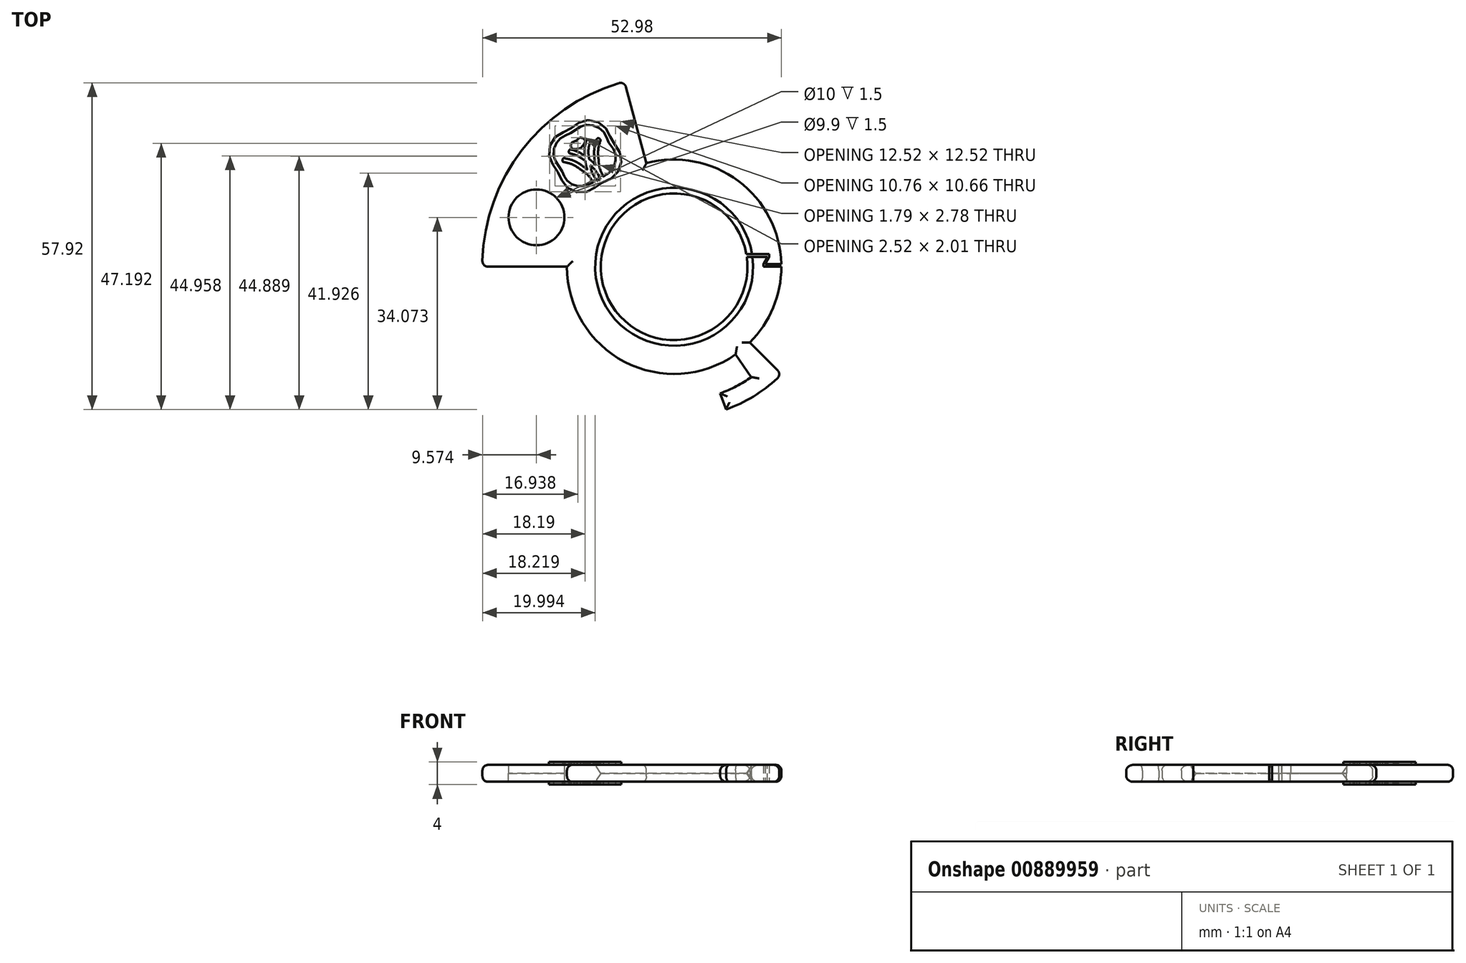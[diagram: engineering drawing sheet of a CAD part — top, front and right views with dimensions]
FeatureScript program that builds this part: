
annotation { "Feature Type Name" : "Feature", "Feature Type Description" : "" }
export const myFeature = defineFeature(function(context is Context, id is Id, definition is map)
    precondition{}
    {
        {
            var Q0;
            Q0=qCreatedBy(makeId("Front.planeOp"),FACE);
            var sketch = newSketch(context, id + "F0", { "sketchPlane" : qUnion([Q0])});
            skLineSegment(sketch, "E0.bottom", {"start": v(-19, 1.5) * mm, "end": v(-14, 1.5) * mm});
            skLineSegment(sketch, "E0.top", {"start": v(-19, 0) * mm, "end": v(-13.96, 0) * mm});
            skLineSegment(sketch, "E0.left", {"start": v(-19, 1.5) * mm, "end": v(-19, 0) * mm});
            skLineSegment(sketch, "E1", {"start": v(-14, 1.5) * mm, "end": v(-13, 0) * mm});
            skLineSegment(sketch, "E2", {"start": v(-13, 0) * mm, "end": v(-13.96, 0) * mm});
            skLineSegment(sketch, "E3.MirrorCS", {"start": v(-19, -1.5) * mm, "end": v(-19, 0) * mm});
            skLineSegment(sketch, "E4.MirrorCS", {"start": v(-19, -1.5) * mm, "end": v(-14, -1.5) * mm});
            skLineSegment(sketch, "E5.MirrorCS", {"start": v(-14, -1.5) * mm, "end": v(-13, 0) * mm});
            skSolve(sketch);
        }
        {
            var Q0;
            Q0=qCreatedBy(makeId("Right.planeOp"),FACE);
            var sketch = newSketch(context, id + "F1", { "sketchPlane" : qUnion([Q0])});
            skLineSegment(sketch, "E6", {"start": v(0, -35.32) * mm, "end": v(0, 30.2) * mm});
            skSolve(sketch);
        }
        {
            var Q0;
            Q0 = qSketchRegion(id + "F0", true);
            var Q1;
            Q1=sQuery(id+"F1.wireOp",EDGE,"E6");
            revolve(context, id + "F2", {"surfaceOperationType" : NewSurfaceOperationType.NEW, "entities" : qUnion([Q0]), "axis" : qUnion([Q1]), "revolveType" : RevolveType.FULL});
        }
        {
            var Q0;
            Q0=qCreatedBy(makeId("Front.planeOp"),FACE);
            var sketch = newSketch(context, id + "F3", { "sketchPlane" : qUnion([Q0])});
            skLineSegment(sketch, "E7.bottom", {"start": v(-34, -1.5) * mm, "end": v(-19, -1.5) * mm});
            skLineSegment(sketch, "E7.top", {"start": v(-34, 1.5) * mm, "end": v(-19, 1.5) * mm});
            skLineSegment(sketch, "E7.left", {"start": v(-34, -1.5) * mm, "end": v(-34, 1.5) * mm});
            skLineSegment(sketch, "E7.right", {"start": v(-19, -1.5) * mm, "end": v(-19, 1.5) * mm});
            skLineSegment(sketch, "E8", {"start": v(19, 1.5) * mm, "end": v(19, -1.5) * mm});
            skSolve(sketch);
        }
        {
            var Q0;
            Q0=qCreatedBy(makeId("Right.planeOp"),FACE);
            var sketch = newSketch(context, id + "F4", { "sketchPlane" : qUnion([Q0])});
            skLineSegment(sketch, "E9", {"start": v(0, 18.48) * mm, "end": v(0, -14.6) * mm});
            skSolve(sketch);
        }
        {
            var Q0;
            Q0 = qSketchRegion(id + "F3", true);
            var Q1;
            Q1=sQuery(id+"F4.wireOp",EDGE,"E9");
            revolve(context, id + "F5", {"operationType" : NewBodyOperationType.ADD, "surfaceOperationType" : NewSurfaceOperationType.NEW, "entities" : qUnion([Q0]), "axis" : qUnion([Q1]), "revolveType" : RevolveType.ONE_DIRECTION, "angle" : 75 * degree});
        }
        {
            var Q0;
            Q0=qCreatedBy(makeId("Top.planeOp"),FACE);
            var sketch = newSketch(context, id + "F6", { "sketchPlane" : qUnion([Q0])});
            skCircle(sketch, "E10", {"center": v(-24.4, 8.75) * mm, "radius": 5 * mm});
            skSolve(sketch);
        }
        {
            var Q0;
            Q0=makeQuery(id+"F5.boolean.opBoolean","MERGE",FACE,{"derivedFrom":[makeQuery(id+"F2.opRevolve","SWEPT_FACE",FACE,{"disambiguationData":[OSD([sQuery(id+"F0.wireOp",EDGE,"E0.bottom")])]}),makeQuery(id+"F5.opRevolve","SWEPT_FACE",FACE,{"disambiguationData":[OSD([sQuery(id+"F3.wireOp",EDGE,"E7.top")])]})]});
            var sketch = newSketch(context, id + "F7", { "sketchPlane" : qUnion([Q0])});
            skLineSegment(sketch, "E11", {"start": v(19, 0) * mm, "end": v(15.82, 0) * mm});
            skLineSegment(sketch, "E12", {"start": v(15.82, 0) * mm, "end": v(16.84, 1.72) * mm});
            skLineSegment(sketch, "E13", {"start": v(16.84, 1.72) * mm, "end": v(11.15, 1.72) * mm});
            skSolve(sketch);
        }
        {
            var Q0;
            Q0 = qSketchRegion(id + "F7", true);
            var Q1;
            Q1=sQuery(id+"F7.wireOp",EDGE,"E13");
            var Q2;
            Q2=sQuery(id+"F7.wireOp",EDGE,"E12");
            var Q3;
            Q3=sQuery(id+"F7.wireOp",EDGE,"E11");
            var Q4;
            Q4=sQuery(id+"F7.wireOp",EDGE,"dRNst7FH-cN4A-1J2b-OH71-uqqUjtxT50Xl");
            extrude(context, id + "F8", {"entities" : qUnion([Q0]), "bodyType" : ToolBodyType.SURFACE, "surfaceEntities" : qUnion([Q1, Q2, Q3, Q4]), "endBound" : BoundingType.SYMMETRIC, "oppositeDirection" : true, "depth" : 18.2 * mm, "offsetDistance" : 25 * mm});
        }
        {
            var Q0;
            Q0=qCreatedBy(makeId("Front.planeOp"),FACE);
            var Q1;
            Q1=qCreatedBy(makeId("Right.planeOp"),FACE);
            cPlane(context, id + "F9", {"entities" : qUnion([Q0, Q1]), "cplaneType" : CPlaneType.MID_PLANE, "offset" : 25 * mm, "width" : 150 * mm, "height" : 150 * mm});
        }
        {
            var Q0;
            Q0=qCreatedBy(id+"F9.planeOp",FACE);
            var sketch = newSketch(context, id + "F10", { "sketchPlane" : qUnion([Q0])});
            skLineSegment(sketch, "E14.bottom", {"start": v(18.75, 1.5) * mm, "end": v(26.94, 1.5) * mm});
            skLineSegment(sketch, "E14.top", {"start": v(18.75, -1.5) * mm, "end": v(26.94, -1.5) * mm});
            skLineSegment(sketch, "E14.left", {"start": v(18.75, 1.5) * mm, "end": v(18.75, -1.5) * mm});
            skLineSegment(sketch, "E14.right", {"start": v(26.94, 1.5) * mm, "end": v(26.94, -1.5) * mm});
            skLineSegment(sketch, "E15", {"start": v(23.89, 1.5) * mm, "end": v(23.89, -1.5) * mm});
            skSolve(sketch);
        }
        {
            var Q0;
            Q0=qCreatedBy(makeId("Front.planeOp"),FACE);
            var sketch = newSketch(context, id + "F11", { "sketchPlane" : qUnion([Q0])});
            skLineSegment(sketch, "E16", {"start": v(0, -32.03) * mm, "end": v(0, 34.42) * mm});
            skSolve(sketch);
        }
        {
            var Q0;
            {var subQ0=sQuery(id+"F10.wireOp",EDGE,"E14.left");Q0=makeQuery(id+"F10.imprint","IMPRINT",FACE,{"disambiguationData":[TD([[makeQuery(id+"F10.imprint","IMPRINT",EDGE,{"derivedFrom":subQ0}),1.0]])]});}
            var Q1;
            Q1=sQuery(id+"F11.wireOp",EDGE,"E16");
            revolve(context, id + "F12", {"operationType" : NewBodyOperationType.ADD, "surfaceOperationType" : NewSurfaceOperationType.NEW, "entities" : qUnion([Q0]), "axis" : qUnion([Q1]), "revolveType" : RevolveType.ONE_DIRECTION, "oppositeDirection" : true, "angle" : 10 * degree});
        }
        {
            var Q0;
            {var subQ0=sQuery(id+"F10.wireOp",EDGE,"E14.right");Q0=makeQuery(id+"F10.imprint","IMPRINT",FACE,{"disambiguationData":[TD([[makeQuery(id+"F10.imprint","IMPRINT",EDGE,{"derivedFrom":subQ0}),-1.0]])]});}
            var Q1;
            Q1=sQuery(id+"F11.wireOp",EDGE,"E16");
            revolve(context, id + "F13", {"operationType" : NewBodyOperationType.ADD, "surfaceOperationType" : NewSurfaceOperationType.NEW, "entities" : qUnion([Q0]), "axis" : qUnion([Q1]), "revolveType" : RevolveType.ONE_DIRECTION, "oppositeDirection" : true, "angle" : 25 * degree});
        }
        {
            var Q0;
            Q0=makeQuery(id+"F8.opExtrude","SWEPT_FACE",FACE,{"disambiguationData":[OSD([sQuery(id+"F7.wireOp",EDGE,"E13")])]});
            var Q1;
            Q1=makeQuery(id+"F8.opExtrude","SWEPT_FACE",FACE,{"disambiguationData":[OSD([sQuery(id+"F7.wireOp",EDGE,"E12")])]});
            var Q2;
            Q2=makeQuery(id+"F8.opExtrude","SWEPT_FACE",FACE,{"disambiguationData":[OSD([sQuery(id+"F7.wireOp",EDGE,"E11"),sQuery(id+"F7.wireOp",EDGE,"dRNst7FH-cN4A-1J2b-OH71-uqqUjtxT50Xl")])]});
            extrude(context, id + "F14", {"entities" : qUnion([Q0, Q1, Q2]), "operationType" : NewBodyOperationType.REMOVE, "oppositeDirection" : true, "depth" : 0.5 * mm, "offsetDistance" : 25 * mm});
        }
        {
            var Q0;
            Q0=sQuery(id+"F6.wireOp",VERTEX,"E10.center");
            var Q1;
            Q1=makeQuery(id+"F2.opRevolve","SWEPT_BODY",BODY,{"disambiguationData":[OSD([sQuery(id+"F0.wireOp",EDGE,"E0.bottom"),sQuery(id+"F0.wireOp",EDGE,"E0.left"),sQuery(id+"F0.wireOp",EDGE,"E1"),sQuery(id+"F0.wireOp",EDGE,"E3.MirrorCS"),sQuery(id+"F0.wireOp",EDGE,"E4.MirrorCS"),sQuery(id+"F0.wireOp",EDGE,"E5.MirrorCS")])]});
            hole(context, id + "F15", {"style" : HoleStyle.SIMPLE, "endStyle" : HoleEndStyle.THROUGH, "holeDiameter" : 10 * mm, "majorDiameter" : 5 * mm, "isTappedThrough" : true, "tappedDepth" : 12 * mm, "tapClearance" : 3, "locations" : qUnion([Q0]), "scope" : qUnion([Q1])});
        }
        {
            var Q0;
            Q0=sQuery(id+"F6.wireOp",VERTEX,"E10.center");
            var Q1;
            Q1=makeQuery(id+"F2.opRevolve","SWEPT_BODY",BODY,{"disambiguationData":[OSD([sQuery(id+"F0.wireOp",EDGE,"E0.bottom"),sQuery(id+"F0.wireOp",EDGE,"E0.left"),sQuery(id+"F0.wireOp",EDGE,"E1"),sQuery(id+"F0.wireOp",EDGE,"E3.MirrorCS"),sQuery(id+"F0.wireOp",EDGE,"E4.MirrorCS"),sQuery(id+"F0.wireOp",EDGE,"E5.MirrorCS")])]});
            hole(context, id + "F16", {"style" : HoleStyle.SIMPLE, "endStyle" : HoleEndStyle.THROUGH, "oppositeDirection" : true, "holeDiameter" : 9.9 * mm, "majorDiameter" : 5 * mm, "isTappedThrough" : true, "tappedDepth" : 12 * mm, "tapClearance" : 3, "locations" : qUnion([Q0]), "scope" : qUnion([Q1])});
        }
        {
            var Q0;
            Q0=makeQuery(id+"F5.opRevolve","CAP_EDGE",EDGE,{"disambiguationData":[OSD([sQuery(id+"F3.wireOp",EDGE,"E7.top")])],"isStart":true});
            var Q1;
            Q1=makeQuery(id+"F5.opRevolve","SWEPT_EDGE",EDGE,{"disambiguationData":[OSD([sQuery(id+"F3.wireOp",EDGE,"E7.top"),sQuery(id+"F3.wireOp",EDGE,"E7.left")])]});
            var Q2;
            Q2=makeQuery(id+"F5.opRevolve","CAP_EDGE",EDGE,{"disambiguationData":[OSD([sQuery(id+"F3.wireOp",EDGE,"E7.top")])],"isStart":false});
            var Q3;
            Q3=makeQuery(id+"F5.opRevolve","CAP_EDGE",EDGE,{"disambiguationData":[OSD([sQuery(id+"F3.wireOp",EDGE,"E7.bottom")])],"isStart":false});
            var Q4;
            Q4=makeQuery(id+"F5.opRevolve","SWEPT_EDGE",EDGE,{"disambiguationData":[OSD([sQuery(id+"F3.wireOp",EDGE,"E7.bottom"),sQuery(id+"F3.wireOp",EDGE,"E7.left")])]});
            var Q5;
            Q5=makeQuery(id+"F5.opRevolve","CAP_EDGE",EDGE,{"disambiguationData":[OSD([sQuery(id+"F3.wireOp",EDGE,"E7.bottom")])],"isStart":true});
            var Q6;
            {var subQ0=sQuery(id+"F3.wireOp",EDGE,"E7.top");var subQ1=sQuery(id+"F0.wireOp",EDGE,"E0.left");var subQ2=sQuery(id+"F0.wireOp",EDGE,"E0.bottom");Q6=makeQuery(id+"F12.boolean.opBoolean","SPLIT",EDGE,{"disambiguationData":[TD([makeQuery(id+"F5.opRevolve","CAP_FACE",FACE,{"disambiguationData":[OSD([sQuery(id+"F3.wireOp",EDGE,"E7.bottom"),subQ0,sQuery(id+"F3.wireOp",EDGE,"E7.left"),sQuery(id+"F3.wireOp",EDGE,"E7.right")])],"isStart":true})])],"derivedFrom":makeQuery(id+"F2.opRevolve","SWEPT_EDGE",EDGE,{"disambiguationData":[OSD([subQ2,subQ1])]})});}
            var Q7;
            {var subQ0=sQuery(id+"F3.wireOp",EDGE,"E7.bottom");var subQ1=sQuery(id+"F0.wireOp",EDGE,"E4.MirrorCS");var subQ2=sQuery(id+"F0.wireOp",EDGE,"E3.MirrorCS");Q7=makeQuery(id+"F12.boolean.opBoolean","SPLIT",EDGE,{"disambiguationData":[TD([makeQuery(id+"F5.opRevolve","CAP_FACE",FACE,{"disambiguationData":[OSD([subQ0,sQuery(id+"F3.wireOp",EDGE,"E7.top"),sQuery(id+"F3.wireOp",EDGE,"E7.left"),sQuery(id+"F3.wireOp",EDGE,"E7.right")])],"isStart":true})])],"derivedFrom":makeQuery(id+"F2.opRevolve","SWEPT_EDGE",EDGE,{"disambiguationData":[OSD([subQ2,subQ1])]})});}
            var Q8;
            {var subQ0=sQuery(id+"F3.wireOp",EDGE,"E7.top");var subQ2=makeQuery(id+"F5.opRevolve","CAP_FACE",FACE,{"disambiguationData":[OSD([sQuery(id+"F3.wireOp",EDGE,"E7.bottom"),subQ0,sQuery(id+"F3.wireOp",EDGE,"E7.left"),sQuery(id+"F3.wireOp",EDGE,"E7.right")])],"isStart":false});var subQ3=sQuery(id+"F0.wireOp",EDGE,"E0.left");var subQ5=sQuery(id+"F0.wireOp",EDGE,"E0.bottom");Q8=makeQuery(id+"F14.boolean.opBoolean","SPLIT",EDGE,{"disambiguationData":[TD([makeQuery(id+"F14.opExtrude","CAP_FACE",FACE,{"disambiguationData":[OSD([sQuery(id+"F7.wireOp",EDGE,"E11")])],"isStart":false})])],"derivedFrom":makeQuery(id+"F12.boolean.opBoolean","SPLIT",EDGE,{"disambiguationData":[TD([subQ2])],"derivedFrom":makeQuery(id+"F2.opRevolve","SWEPT_EDGE",EDGE,{"disambiguationData":[OSD([subQ5,subQ3])]})})});}
            var Q9;
            {var subQ0=sQuery(id+"F3.wireOp",EDGE,"E7.bottom");var subQ2=sQuery(id+"F0.wireOp",EDGE,"E4.MirrorCS");var subQ4=makeQuery(id+"F5.opRevolve","CAP_FACE",FACE,{"disambiguationData":[OSD([subQ0,sQuery(id+"F3.wireOp",EDGE,"E7.top"),sQuery(id+"F3.wireOp",EDGE,"E7.left"),sQuery(id+"F3.wireOp",EDGE,"E7.right")])],"isStart":false});var subQ5=sQuery(id+"F0.wireOp",EDGE,"E3.MirrorCS");Q9=makeQuery(id+"F14.boolean.opBoolean","SPLIT",EDGE,{"disambiguationData":[TD([makeQuery(id+"F14.opExtrude","CAP_FACE",FACE,{"disambiguationData":[OSD([sQuery(id+"F7.wireOp",EDGE,"E11")])],"isStart":false})])],"derivedFrom":makeQuery(id+"F12.boolean.opBoolean","SPLIT",EDGE,{"disambiguationData":[TD([subQ4])],"derivedFrom":makeQuery(id+"F2.opRevolve","SWEPT_EDGE",EDGE,{"disambiguationData":[OSD([subQ5,subQ2])]})})});}
            var Q10;
            {var subQ0=sQuery(id+"F3.wireOp",EDGE,"E7.top");var subQ4=sQuery(id+"F0.wireOp",EDGE,"E0.left");var subQ6=sQuery(id+"F0.wireOp",EDGE,"E0.bottom");Q10=makeQuery(id+"F14.boolean.opBoolean","SPLIT",EDGE,{"disambiguationData":[TD([makeQuery(id+"F14.opExtrude","CAP_FACE",FACE,{"disambiguationData":[OSD([sQuery(id+"F7.wireOp",EDGE,"E11")])],"isStart":true})])],"derivedFrom":makeQuery(id+"F12.boolean.opBoolean","SPLIT",EDGE,{"disambiguationData":[TD([makeQuery(id+"F5.opRevolve","CAP_FACE",FACE,{"disambiguationData":[OSD([sQuery(id+"F3.wireOp",EDGE,"E7.bottom"),subQ0,sQuery(id+"F3.wireOp",EDGE,"E7.left"),sQuery(id+"F3.wireOp",EDGE,"E7.right")])],"isStart":false})])],"derivedFrom":makeQuery(id+"F2.opRevolve","SWEPT_EDGE",EDGE,{"disambiguationData":[OSD([subQ6,subQ4])]})})});}
            var Q11;
            {var subQ4=sQuery(id+"F3.wireOp",EDGE,"E7.bottom");var subQ6=sQuery(id+"F0.wireOp",EDGE,"E4.MirrorCS");var subQ8=sQuery(id+"F0.wireOp",EDGE,"E3.MirrorCS");Q11=makeQuery(id+"F14.boolean.opBoolean","SPLIT",EDGE,{"disambiguationData":[TD([makeQuery(id+"F14.opExtrude","CAP_FACE",FACE,{"disambiguationData":[OSD([sQuery(id+"F7.wireOp",EDGE,"E11")])],"isStart":true})])],"derivedFrom":makeQuery(id+"F12.boolean.opBoolean","SPLIT",EDGE,{"disambiguationData":[TD([makeQuery(id+"F5.opRevolve","CAP_FACE",FACE,{"disambiguationData":[OSD([subQ4,sQuery(id+"F3.wireOp",EDGE,"E7.top"),sQuery(id+"F3.wireOp",EDGE,"E7.left"),sQuery(id+"F3.wireOp",EDGE,"E7.right")])],"isStart":false})])],"derivedFrom":makeQuery(id+"F2.opRevolve","SWEPT_EDGE",EDGE,{"disambiguationData":[OSD([subQ8,subQ6])]})})});}
            var Q12;
            Q12=makeQuery(id+"F12.opRevolve","CAP_EDGE",EDGE,{"disambiguationData":[OSD([sQuery(id+"F10.wireOp",EDGE,"E14.bottom")])],"isStart":false});
            var Q13;
            Q13=makeQuery(id+"F13.opRevolve","SWEPT_EDGE",EDGE,{"disambiguationData":[OSD([sQuery(id+"F10.wireOp",EDGE,"E14.bottom"),sQuery(id+"F10.wireOp",EDGE,"E15")])]});
            var Q14;
            Q14=makeQuery(id+"F13.opRevolve","CAP_EDGE",EDGE,{"disambiguationData":[OSD([sQuery(id+"F10.wireOp",EDGE,"E14.bottom")])],"isStart":false});
            var Q15;
            Q15=makeQuery(id+"F13.opRevolve","SWEPT_EDGE",EDGE,{"disambiguationData":[OSD([sQuery(id+"F10.wireOp",EDGE,"E14.bottom"),sQuery(id+"F10.wireOp",EDGE,"E14.right")])]});
            var Q16;
            {var subQ0=sQuery(id+"F10.wireOp",EDGE,"E14.bottom");Q16=makeQuery(id+"F13.boolean.opBoolean","MERGE",EDGE,{"derivedFrom":[makeQuery(id+"F12.opRevolve","CAP_EDGE",EDGE,{"disambiguationData":[OSD([subQ0])],"isStart":true}),makeQuery(id+"F13.opRevolve","CAP_EDGE",EDGE,{"disambiguationData":[OSD([subQ0])],"isStart":true})]});}
            var Q17;
            Q17=makeQuery(id+"F13.opRevolve","CAP_EDGE",EDGE,{"disambiguationData":[OSD([sQuery(id+"F10.wireOp",EDGE,"E14.top")])],"isStart":false});
            var Q18;
            Q18=makeQuery(id+"F13.opRevolve","SWEPT_EDGE",EDGE,{"disambiguationData":[OSD([sQuery(id+"F10.wireOp",EDGE,"E14.top"),sQuery(id+"F10.wireOp",EDGE,"E14.right")])]});
            var Q19;
            {var subQ0=sQuery(id+"F10.wireOp",EDGE,"E14.top");Q19=makeQuery(id+"F13.boolean.opBoolean","MERGE",EDGE,{"derivedFrom":[makeQuery(id+"F12.opRevolve","CAP_EDGE",EDGE,{"disambiguationData":[OSD([subQ0])],"isStart":true}),makeQuery(id+"F13.opRevolve","CAP_EDGE",EDGE,{"disambiguationData":[OSD([subQ0])],"isStart":true})]});}
            var Q20;
            Q20=makeQuery(id+"F12.opRevolve","CAP_EDGE",EDGE,{"disambiguationData":[OSD([sQuery(id+"F10.wireOp",EDGE,"E14.top")])],"isStart":false});
            var Q21;
            Q21=makeQuery(id+"F13.opRevolve","SWEPT_EDGE",EDGE,{"disambiguationData":[OSD([sQuery(id+"F10.wireOp",EDGE,"E14.top"),sQuery(id+"F10.wireOp",EDGE,"E15")])]});
            var Q22;
            Q22=makeQuery(id+"F5.opRevolve","CAP_EDGE",EDGE,{"disambiguationData":[OSD([sQuery(id+"F3.wireOp",EDGE,"E7.left")])],"isStart":false});
            var Q23;
            Q23=makeQuery(id+"F5.opRevolve","CAP_EDGE",EDGE,{"disambiguationData":[OSD([sQuery(id+"F3.wireOp",EDGE,"E7.left")])],"isStart":true});
            var Q24;
            Q24=makeQuery(id+"F13.opRevolve","CAP_EDGE",EDGE,{"disambiguationData":[OSD([sQuery(id+"F10.wireOp",EDGE,"E14.right")])],"isStart":true});
            fillet(context, id + "F17", {"entities" : qUnion([Q0, Q1, Q2, Q3, Q4, Q5, Q6, Q7, Q8, Q9, Q10, Q11, Q12, Q13, Q14, Q15, Q16, Q17, Q18, Q19, Q20, Q21, Q22, Q23, Q24]), "radius" : 1 * mm, "tangentPropagation" : true, "allowEdgeOverflow" : false});
        }
        {
            var Q0;
            Q0=qCreatedBy(makeId("Top.planeOp"),FACE);
            var sketch = newSketch(context, id + "F18", { "sketchPlane" : qUnion([Q0])});
            skFitSpline(sketch, "E17", {"points": [v(-17.74, 22.2) * mm, v(-18.18, 21.95) * mm, v(-18.19, 21.04) * mm, v(-16.6, 21.01) * mm]});
            skFitSpline(sketch, "E18", {"points": [v(-16.6, 21.01) * mm, v(-16.6, 21.02) * mm, v(-16.6, 21.02) * mm, v(-16.6, 21.02) * mm, v(-16.6, 21.02) * mm, v(-16.6, 21.02) * mm, v(-16.6, 21.02) * mm]});
            skFitSpline(sketch, "E19", {"points": [v(-16.6, 21.02) * mm, v(-15.8, 22.44) * mm, v(-16.68, 22.88) * mm, v(-17.1, 22.56) * mm]});
            skFitSpline(sketch, "E20", {"points": [v(-17.1, 22.56) * mm, v(-17.26, 22.44) * mm, v(-17.29, 22.3) * mm, v(-17.28, 22.19) * mm]});
            skFitSpline(sketch, "E21", {"points": [v(-17.28, 22.19) * mm, v(-17.37, 22.25) * mm, v(-17.5, 22.3) * mm, v(-17.7, 22.22) * mm]});
            skFitSpline(sketch, "E22", {"points": [v(-17.7, 22.22) * mm, v(-17.7, 22.21) * mm, v(-17.72, 22.2) * mm, v(-17.73, 22.2) * mm, v(-17.74, 22.2) * mm, v(-17.74, 22.2) * mm, v(-17.74, 22.2) * mm, v(-17.74, 22.2) * mm, v(-17.74, 22.2) * mm, v(-17.74, 22.2) * mm]});
            skFitSpline(sketch, "E23", {"points": [v(-20.6, 16.8) * mm, v(-19.07, 14.15) * mm, v(-15.67, 13.23) * mm, v(-13.02, 14.76) * mm, v(-10.37, 16.3) * mm, v(-9.45, 19.7) * mm, v(-10.98, 22.34) * mm, v(-12.51, 25) * mm, v(-15.91, 25.9) * mm, v(-18.56, 24.38) * mm, v(-21.21, 22.85) * mm, v(-22.13, 19.44) * mm, v(-20.6, 16.8) * mm]});
            skFitSpline(sketch, "E24", {"points": [v(-13.1, 15.55) * mm, v(-13.18, 15.49) * mm, v(-13.27, 15.43) * mm, v(-13.37, 15.37) * mm, v(-13.46, 15.31) * mm, v(-13.57, 15.27) * mm, v(-13.67, 15.22) * mm]});
            skFitSpline(sketch, "E25", {"points": [v(-13.67, 15.22) * mm, v(-14.1, 15.9) * mm, v(-14.59, 16.83) * mm, v(-14.88, 18) * mm]});
            skFitSpline(sketch, "E26", {"points": [v(-14.88, 18) * mm, v(-14.02, 17.16) * mm, v(-13.45, 16.26) * mm, v(-13.1, 15.55) * mm]});
            skFitSpline(sketch, "E27", {"points": [v(-11.6, 22) * mm, v(-10.43, 19.98) * mm, v(-10.88, 17.48) * mm, v(-12.53, 15.98) * mm]});
            skFitSpline(sketch, "E28", {"points": [v(-12.53, 15.98) * mm, v(-12.54, 16) * mm, v(-12.54, 16) * mm, v(-12.55, 16.01) * mm]});
            skFitSpline(sketch, "E29", {"points": [v(-12.55, 16.01) * mm, v(-12.55, 16.02) * mm, v(-12.55, 16.04) * mm, v(-12.56, 16.05) * mm]});
            skFitSpline(sketch, "E30", {"points": [v(-12.56, 16.05) * mm, v(-13.02, 17) * mm, v(-13.3, 18.01) * mm, v(-13.4, 19.07) * mm]});
            skFitSpline(sketch, "E31", {"points": [v(-13.4, 19.07) * mm, v(-13.48, 20.16) * mm, v(-13.38, 21.25) * mm, v(-13.07, 22.3) * mm]});
            skFitSpline(sketch, "E32", {"points": [v(-13.07, 22.3) * mm, v(-13.04, 22.4) * mm, v(-13.06, 22.5) * mm, v(-13.1, 22.58) * mm, v(-13.15, 22.66) * mm, v(-13.22, 22.72) * mm, v(-13.31, 22.74) * mm]});
            skFitSpline(sketch, "E33", {"points": [v(-13.31, 22.74) * mm, v(-13.5, 22.8) * mm, v(-13.7, 22.69) * mm, v(-13.74, 22.5) * mm]});
            skFitSpline(sketch, "E34", {"points": [v(-13.74, 22.5) * mm, v(-14.07, 21.37) * mm, v(-14.19, 20.2) * mm, v(-14.1, 19.01) * mm]});
            skFitSpline(sketch, "E35", {"points": [v(-14.1, 19.01) * mm, v(-14.06, 18.68) * mm, v(-14.01, 18.36) * mm, v(-13.95, 18.03) * mm]});
            skFitSpline(sketch, "E36", {"points": [v(-13.95, 18.03) * mm, v(-14.28, 18.4) * mm, v(-14.65, 18.76) * mm, v(-15.08, 19.1) * mm]});
            skFitSpline(sketch, "E37", {"points": [v(-15.08, 19.1) * mm, v(-15.09, 19.17) * mm, v(-15.1, 19.22) * mm, v(-15.1, 19.28) * mm]});
            skFitSpline(sketch, "E38", {"points": [v(-15.1, 19.28) * mm, v(-15.2, 20.2) * mm, v(-15.14, 21.14) * mm, v(-14.92, 22.05) * mm]});
            skFitSpline(sketch, "E39", {"points": [v(-14.92, 22.05) * mm, v(-14.9, 22.14) * mm, v(-14.92, 22.23) * mm, v(-14.96, 22.3) * mm, v(-15, 22.39) * mm, v(-15.09, 22.45) * mm, v(-15.18, 22.47) * mm]});
            skFitSpline(sketch, "E40", {"points": [v(-15.18, 22.47) * mm, v(-15.37, 22.51) * mm, v(-15.56, 22.4) * mm, v(-15.6, 22.2) * mm]});
            skFitSpline(sketch, "E41", {"points": [v(-15.6, 22.2) * mm, v(-15.8, 21.37) * mm, v(-15.87, 20.5) * mm, v(-15.83, 19.64) * mm]});
            skFitSpline(sketch, "E42", {"points": [v(-15.83, 19.64) * mm, v(-16.56, 20.12) * mm, v(-17.35, 20.5) * mm, v(-18.2, 20.76) * mm]});
            skFitSpline(sketch, "E43", {"points": [v(-18.2, 20.76) * mm, v(-18.38, 20.81) * mm, v(-18.57, 20.7) * mm, v(-18.63, 20.52) * mm]});
            skFitSpline(sketch, "E44", {"points": [v(-18.63, 20.52) * mm, v(-18.69, 20.34) * mm, v(-18.58, 20.14) * mm, v(-18.4, 20.09) * mm]});
            skFitSpline(sketch, "E45", {"points": [v(-18.4, 20.09) * mm, v(-17.5, 19.82) * mm, v(-16.66, 19.4) * mm, v(-15.9, 18.86) * mm]});
            skFitSpline(sketch, "E46", {"points": [v(-15.9, 18.86) * mm, v(-15.85, 18.82) * mm, v(-15.8, 18.77) * mm, v(-15.73, 18.73) * mm]});
            skFitSpline(sketch, "E47", {"points": [v(-15.73, 18.73) * mm, v(-15.65, 18.17) * mm, v(-15.53, 17.65) * mm, v(-15.37, 17.18) * mm]});
            skFitSpline(sketch, "E48", {"points": [v(-15.37, 17.18) * mm, v(-15.62, 17.4) * mm, v(-15.87, 17.6) * mm, v(-16.15, 17.78) * mm]});
            skFitSpline(sketch, "E49", {"points": [v(-16.15, 17.78) * mm, v(-17.12, 18.46) * mm, v(-18.2, 18.94) * mm, v(-19.34, 19.23) * mm]});
            skFitSpline(sketch, "E50", {"points": [v(-19.34, 19.23) * mm, v(-19.53, 19.27) * mm, v(-19.72, 19.16) * mm, v(-19.77, 18.97) * mm]});
            skFitSpline(sketch, "E51", {"points": [v(-19.77, 18.97) * mm, v(-19.81, 18.79) * mm, v(-19.7, 18.6) * mm, v(-19.51, 18.55) * mm]});
            skFitSpline(sketch, "E52", {"points": [v(-19.51, 18.55) * mm, v(-18.45, 18.28) * mm, v(-17.45, 17.83) * mm, v(-16.54, 17.2) * mm]});
            skFitSpline(sketch, "E53", {"points": [v(-16.54, 17.2) * mm, v(-15.68, 16.6) * mm, v(-14.94, 15.85) * mm, v(-14.35, 14.97) * mm, v(-14.34, 14.97) * mm, v(-14.34, 14.97) * mm, v(-14.34, 14.97) * mm]});
            skFitSpline(sketch, "E54", {"points": [v(-14.34, 14.97) * mm, v(-14.33, 14.96) * mm, v(-14.33, 14.95) * mm, v(-14.33, 14.95) * mm]});
            skFitSpline(sketch, "E55", {"points": [v(-14.33, 14.95) * mm, v(-16.45, 14.28) * mm, v(-18.83, 15.14) * mm, v(-19.99, 17.14) * mm, v(-21.33, 19.46) * mm, v(-20.53, 22.43) * mm, v(-18.21, 23.77) * mm, v(-15.9, 25.1) * mm, v(-12.93, 24.31) * mm, v(-11.6, 22) * mm]});
            skSolve(sketch);
        }
        {
            var Q0;
            Q0=makeQuery(id+"F18.imprint","IMPRINT",FACE,{"disambiguationData":[TD([[makeQuery(id+"F18.imprint","IMPRINT",EDGE,{"derivedFrom":sQuery(id+"F18.wireOp",EDGE,"E23")}),1.0]])]});
            var Q1;
            Q1=makeQuery(id+"F18.imprint","IMPRINT",FACE,{"disambiguationData":[TD([[makeQuery(id+"F18.imprint","IMPRINT",EDGE,{"derivedFrom":sQuery(id+"F18.wireOp",EDGE,"E17")}),1.0]])]});
            extrude(context, id + "F19", {"entities" : qUnion([Q0, Q1]), "operationType" : NewBodyOperationType.ADD, "oppositeDirection" : true, "depth" : 2 * mm, "offsetDistance" : 25 * mm});
        }
        {
            var Q0;
            Q0=makeQuery(id+"F19.opExtrude","CAP_FACE",FACE,{"disambiguationData":[OSD([sQuery(id+"F18.wireOp",EDGE,"E23"),sQuery(id+"F18.wireOp",EDGE,"E24"),sQuery(id+"F18.wireOp",EDGE,"E25"),sQuery(id+"F18.wireOp",EDGE,"E26"),sQuery(id+"F18.wireOp",EDGE,"E27"),sQuery(id+"F18.wireOp",EDGE,"E28"),sQuery(id+"F18.wireOp",EDGE,"E29"),sQuery(id+"F18.wireOp",EDGE,"E30"),sQuery(id+"F18.wireOp",EDGE,"E31"),sQuery(id+"F18.wireOp",EDGE,"E32"),sQuery(id+"F18.wireOp",EDGE,"E33"),sQuery(id+"F18.wireOp",EDGE,"E34"),sQuery(id+"F18.wireOp",EDGE,"E35"),sQuery(id+"F18.wireOp",EDGE,"E36"),sQuery(id+"F18.wireOp",EDGE,"E37"),sQuery(id+"F18.wireOp",EDGE,"E38"),sQuery(id+"F18.wireOp",EDGE,"E39"),sQuery(id+"F18.wireOp",EDGE,"E40"),sQuery(id+"F18.wireOp",EDGE,"E41"),sQuery(id+"F18.wireOp",EDGE,"E42"),sQuery(id+"F18.wireOp",EDGE,"E43"),sQuery(id+"F18.wireOp",EDGE,"E44"),sQuery(id+"F18.wireOp",EDGE,"E45"),sQuery(id+"F18.wireOp",EDGE,"E46"),sQuery(id+"F18.wireOp",EDGE,"E47"),sQuery(id+"F18.wireOp",EDGE,"E48"),sQuery(id+"F18.wireOp",EDGE,"E49"),sQuery(id+"F18.wireOp",EDGE,"E50"),sQuery(id+"F18.wireOp",EDGE,"E51"),sQuery(id+"F18.wireOp",EDGE,"E52"),sQuery(id+"F18.wireOp",EDGE,"E53"),sQuery(id+"F18.wireOp",EDGE,"E54"),sQuery(id+"F18.wireOp",EDGE,"E55")])],"isStart":false});
            var Q1;
            Q1=makeQuery(id+"F19.opExtrude","CAP_FACE",FACE,{"disambiguationData":[OSD([sQuery(id+"F18.wireOp",EDGE,"E17"),sQuery(id+"F18.wireOp",EDGE,"E18"),sQuery(id+"F18.wireOp",EDGE,"E19"),sQuery(id+"F18.wireOp",EDGE,"E20"),sQuery(id+"F18.wireOp",EDGE,"E21"),sQuery(id+"F18.wireOp",EDGE,"E22")])],"isStart":false});
            extrude(context, id + "F20", {"entities" : qUnion([Q0, Q1]), "operationType" : NewBodyOperationType.ADD, "oppositeDirection" : true, "depth" : 4 * mm, "offsetDistance" : 25 * mm});
        }
    });
